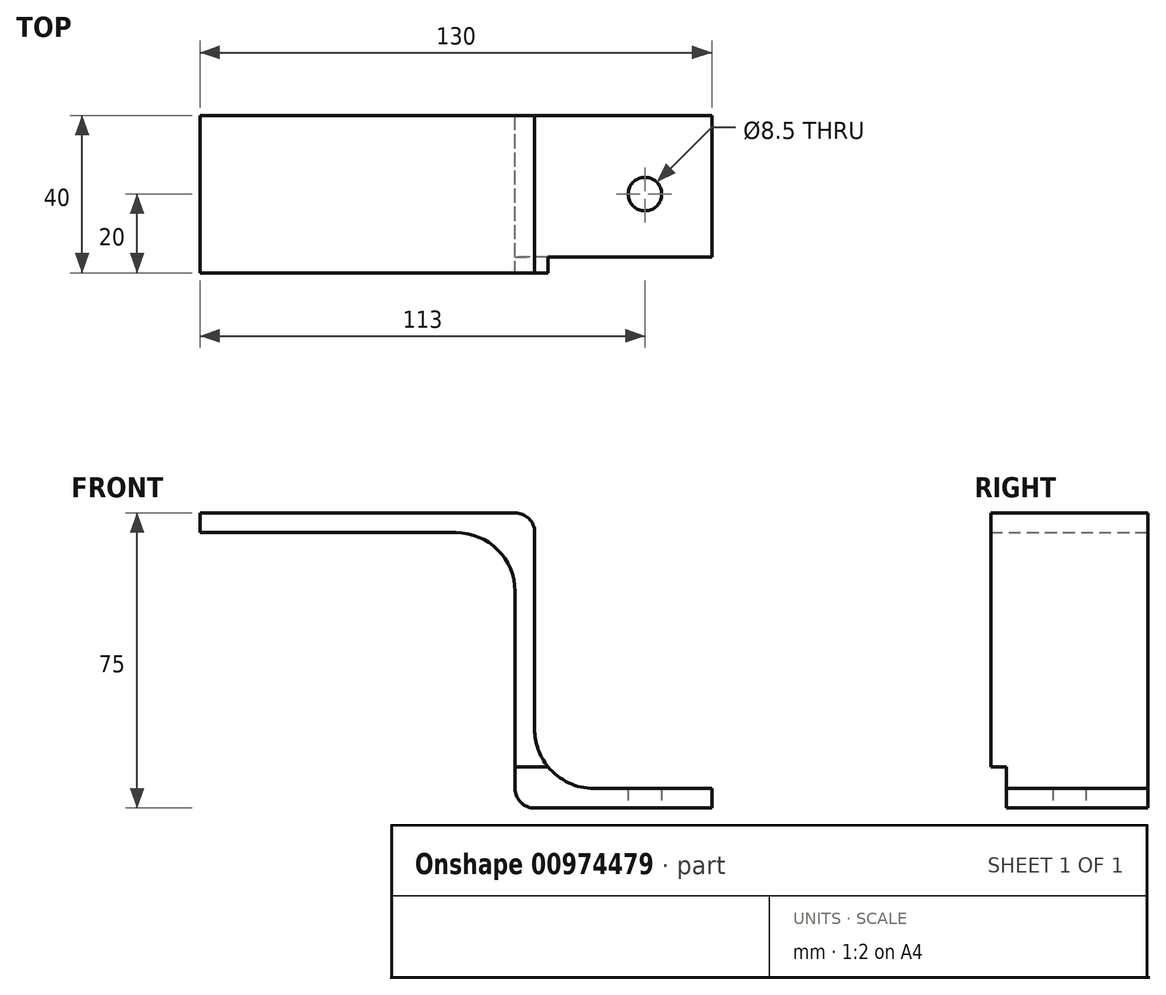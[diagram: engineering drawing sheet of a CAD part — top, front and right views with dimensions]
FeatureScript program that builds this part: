
annotation { "Feature Type Name" : "Feature", "Feature Type Description" : "" }
export const myFeature = defineFeature(function(context is Context, id is Id, definition is map)
    precondition{}
    {
        {
            var Q0;
            Q0=qCreatedBy(makeId("Front.planeOp"),FACE);
            var sketch = newSketch(context, id + "F0", { "sketchPlane" : qUnion([Q0])});
            skLineSegment(sketch, "E0.bottom", {"start": v(0, 0) * mm, "end": v(-45, 0) * mm});
            skLineSegment(sketch, "E0.top", {"start": v(0, 5) * mm, "end": v(-45, 5) * mm});
            skLineSegment(sketch, "E0.left", {"start": v(0, 0) * mm, "end": v(0, 5) * mm});
            skLineSegment(sketch, "E1.bottom", {"start": v(-45, 0) * mm, "end": v(-50, 0) * mm});
            skLineSegment(sketch, "E1.left", {"start": v(-45, 5) * mm, "end": v(-45, 70) * mm});
            skLineSegment(sketch, "E1.right", {"start": v(-50, 0) * mm, "end": v(-50, 70) * mm});
            skLineSegment(sketch, "E2.bottom", {"start": v(-50, 70) * mm, "end": v(-125, 70) * mm});
            skLineSegment(sketch, "E2.top", {"start": v(-45, 75) * mm, "end": v(-125, 75) * mm});
            skLineSegment(sketch, "E2.left", {"start": v(-45, 70) * mm, "end": v(-45, 75) * mm});
            skLineSegment(sketch, "E2.right", {"start": v(-125, 70) * mm, "end": v(-125, 75) * mm});
            skPoint(sketch, "E3", {"position": v(-50, 70) * mm});
            skPoint(sketch, "E4", {"position": v(-45, 5) * mm});
            skSolve(sketch);
        }
        {
            var Q0;
            Q0 = qSketchRegion(id + "F0", true);
            extrude(context, id + "F1", {"entities" : qUnion([Q0]), "depth" : 40 * mm, "offsetDistance" : 25 * mm});
        }
        {
            var Q0;
            Q0=makeQuery(id+"F1.opExtrude","SWEPT_FACE",FACE,{"disambiguationData":[OSD([sQuery(id+"F0.wireOp",EDGE,"E0.bottom"),sQuery(id+"F0.wireOp",EDGE,"E1.bottom")])]});
            var sketch = newSketch(context, id + "F2", { "sketchPlane" : qUnion([Q0])});
            skPoint(sketch, "E5", {"position": v(-17, 20) * mm});
            skCircle(sketch, "E6", {"center": v(-17, 20) * mm, "radius": 4.25 * mm});
            skSolve(sketch);
        }
        {
            var Q0;
            Q0 = qSketchRegion(id + "F2", true);
            extrude(context, id + "F3", {"entities" : qUnion([Q0]), "operationType" : NewBodyOperationType.REMOVE, "oppositeDirection" : true, "depth" : 25 * mm, "offsetDistance" : 25 * mm});
        }
        {
            var Q0;
            Q0=makeQuery(id+"F1.opExtrude","SWEPT_EDGE",EDGE,{"disambiguationData":[OSD([sQuery(id+"F0.wireOp",EDGE,"E0.top"),sQuery(id+"F0.wireOp",EDGE,"E1.left")])]});
            var Q1;
            Q1=makeQuery(id+"F1.opExtrude","SWEPT_EDGE",EDGE,{"disambiguationData":[OSD([sQuery(id+"F0.wireOp",EDGE,"E1.right"),sQuery(id+"F0.wireOp",EDGE,"E2.bottom")])]});
            fillet(context, id + "F4", {"entities" : qUnion([Q0, Q1]), "radius" : 15 * mm, "tangentPropagation" : true, "allowEdgeOverflow" : false});
        }
        {
            var Q0;
            Q0=makeQuery(id+"F1.opExtrude","SWEPT_EDGE",EDGE,{"disambiguationData":[OSD([sQuery(id+"F0.wireOp",EDGE,"E2.top"),sQuery(id+"F0.wireOp",EDGE,"E2.left")])]});
            var Q1;
            Q1=makeQuery(id+"F1.opExtrude","SWEPT_EDGE",EDGE,{"disambiguationData":[OSD([sQuery(id+"F0.wireOp",EDGE,"E1.bottom"),sQuery(id+"F0.wireOp",EDGE,"E1.right")])]});
            fillet(context, id + "F5", {"entities" : qUnion([Q0, Q1]), "radius" : 5 * mm, "tangentPropagation" : true, "allowEdgeOverflow" : false});
        }
        {
            var Q0;
            Q0=makeQuery(id+"F1.opExtrude","CAP_FACE",FACE,{"disambiguationData":[OSD([sQuery(id+"F0.wireOp",EDGE,"E0.bottom"),sQuery(id+"F0.wireOp",EDGE,"E0.top"),sQuery(id+"F0.wireOp",EDGE,"E0.left"),sQuery(id+"F0.wireOp",EDGE,"E1.bottom"),sQuery(id+"F0.wireOp",EDGE,"E1.left"),sQuery(id+"F0.wireOp",EDGE,"E1.right"),sQuery(id+"F0.wireOp",EDGE,"E2.bottom"),sQuery(id+"F0.wireOp",EDGE,"E2.top"),sQuery(id+"F0.wireOp",EDGE,"E2.left"),sQuery(id+"F0.wireOp",EDGE,"E2.right")])],"isStart":false});
            var sketch = newSketch(context, id + "F6", { "sketchPlane" : qUnion([Q0])});
            skLineSegment(sketch, "E7.bottom", {"start": v(0, 0) * mm, "end": v(-56.8, 0) * mm});
            skLineSegment(sketch, "E7.top", {"start": v(0, 10.5) * mm, "end": v(-56.8, 10.5) * mm});
            skLineSegment(sketch, "E7.left", {"start": v(0, 0) * mm, "end": v(0, 10.5) * mm});
            skLineSegment(sketch, "E7.right", {"start": v(-56.8, 0) * mm, "end": v(-56.8, 10.5) * mm});
            skSolve(sketch);
        }
        {
            var Q0;
            Q0 = qSketchRegion(id + "F6", true);
            extrude(context, id + "F7", {"entities" : qUnion([Q0]), "operationType" : NewBodyOperationType.REMOVE, "oppositeDirection" : true, "depth" : 4 * mm, "offsetDistance" : 25 * mm});
        }
        {
            var Q0;
            Q0=makeQuery(id+"F1.opExtrude","SWEPT_FACE",FACE,{"disambiguationData":[OSD([sQuery(id+"F0.wireOp",EDGE,"E2.right")])]});
            extrude(context, id + "F8", {"entities" : qUnion([Q0]), "operationType" : NewBodyOperationType.ADD, "depth" : 5 * mm, "offsetDistance" : 25 * mm});
        }
    });
